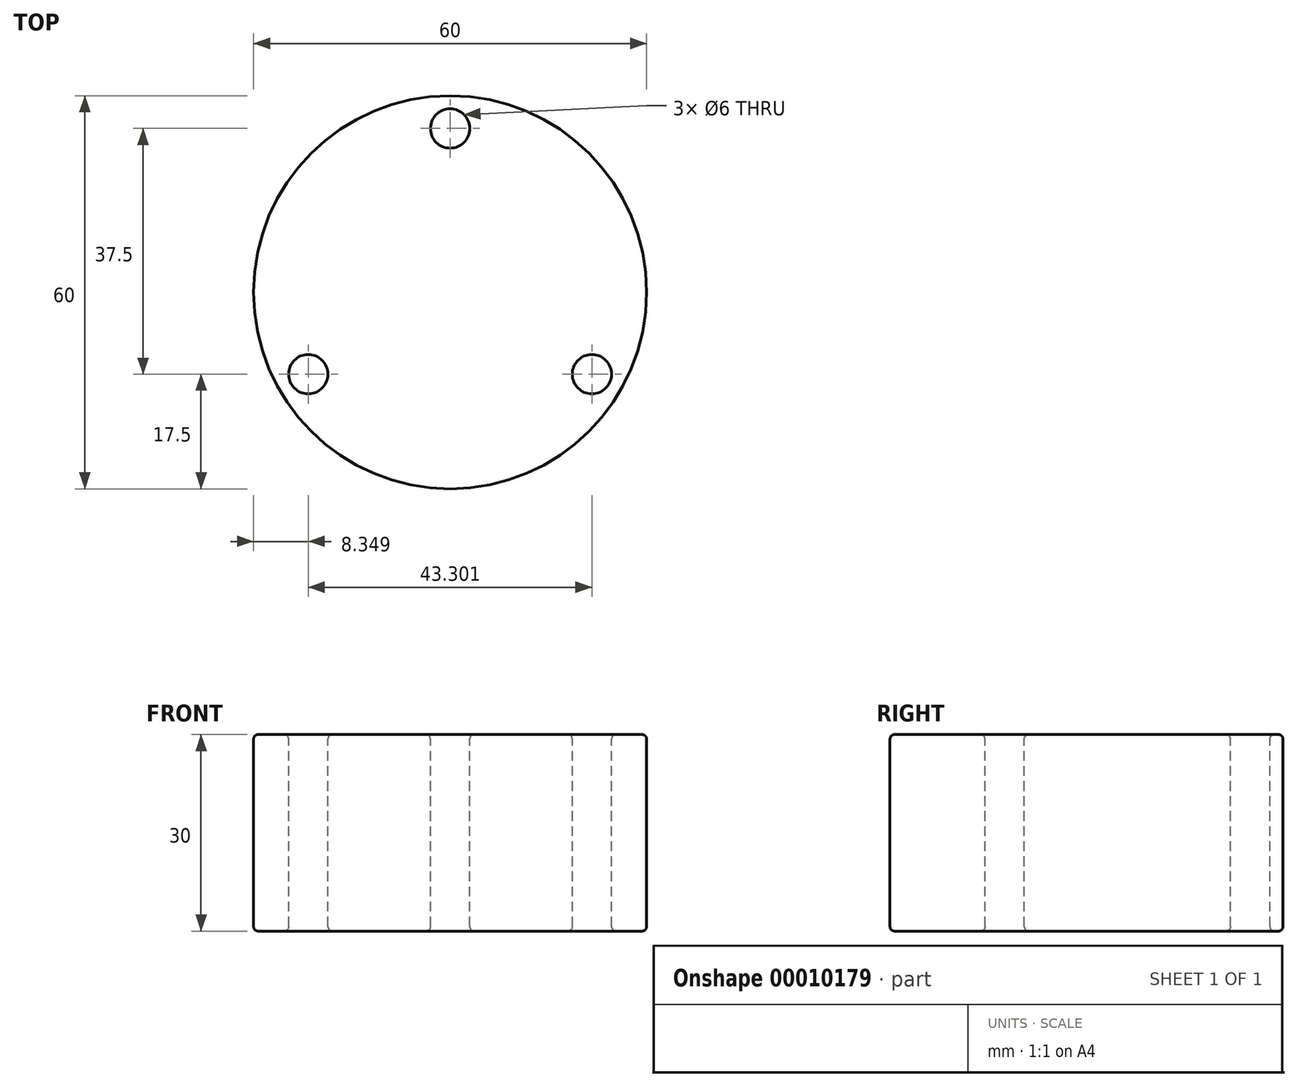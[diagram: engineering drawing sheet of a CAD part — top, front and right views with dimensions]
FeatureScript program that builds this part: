
annotation { "Feature Type Name" : "Feature", "Feature Type Description" : "" }
export const myFeature = defineFeature(function(context is Context, id is Id, definition is map)
    precondition{}
    {
        {
            var Q0;
            Q0=qCreatedBy(makeId("Top.planeOp"),FACE);
            var sketch = newSketch(context, id + "F0", { "sketchPlane" : qUnion([Q0])});
            skCircle(sketch, "E0", {"center": v(0, 0) * mm, "radius": 30 * mm});
            skCircle(sketch, "E1", {"center": v(0, 25) * mm, "radius": 3 * mm});
            skCircle(sketch, "E2.1.0", {"center": v(-21.65, -12.5) * mm, "radius": 3 * mm});
            skCircle(sketch, "E2.2.0", {"center": v(21.65, -12.5) * mm, "radius": 3 * mm});
            skSolve(sketch);
        }
        {
            var Q0;
            Q0=makeQuery(id+"F0.imprint","IMPRINT",FACE,{"disambiguationData":[TD([[makeQuery(id+"F0.imprint","IMPRINT",EDGE,{"derivedFrom":sQuery(id+"F0.wireOp",EDGE,"E0")}),1.0]])]});
            var Q1;
            Q1=sQuery(id+"F0.wireOp",EDGE,"E0");
            extrude(context, id + "F1", {"entities" : qUnion([Q0]), "surfaceEntities" : qUnion([Q1]), "oppositeDirection" : true, "depth" : 30 * mm});
        }
        {
            var Q0;
            Q0=makeQuery(id+"F1.opExtrude","CAP_EDGE",EDGE,{"disambiguationData":[OSD([sQuery(id+"F0.wireOp",EDGE,"E0")])],"isStart":true});
            var Q1;
            Q1=makeQuery(id+"F1.opExtrude","CAP_EDGE",EDGE,{"disambiguationData":[OSD([sQuery(id+"F0.wireOp",EDGE,"E2.1.0")])],"isStart":true});
            var Q2;
            Q2=makeQuery(id+"F1.opExtrude","CAP_EDGE",EDGE,{"disambiguationData":[OSD([sQuery(id+"F0.wireOp",EDGE,"E2.2.0")])],"isStart":true});
            var Q3;
            Q3=makeQuery(id+"F1.opExtrude","CAP_EDGE",EDGE,{"disambiguationData":[OSD([sQuery(id+"F0.wireOp",EDGE,"E1")])],"isStart":true});
            var Q4;
            Q4=makeQuery(id+"F1.opExtrude","CAP_EDGE",EDGE,{"disambiguationData":[OSD([sQuery(id+"F0.wireOp",EDGE,"E0")])],"isStart":false});
            var Q5;
            Q5=makeQuery(id+"F1.opExtrude","CAP_EDGE",EDGE,{"disambiguationData":[OSD([sQuery(id+"F0.wireOp",EDGE,"E2.1.0")])],"isStart":false});
            var Q6;
            Q6=makeQuery(id+"F1.opExtrude","CAP_EDGE",EDGE,{"disambiguationData":[OSD([sQuery(id+"F0.wireOp",EDGE,"E1")])],"isStart":false});
            var Q7;
            Q7=makeQuery(id+"F1.opExtrude","CAP_EDGE",EDGE,{"disambiguationData":[OSD([sQuery(id+"F0.wireOp",EDGE,"E2.2.0")])],"isStart":false});
            fillet(context, id + "F2", {"entities" : qUnion([Q0, Q1, Q2, Q3, Q4, Q5, Q6, Q7]), "radius" : 0.7 * mm, "tangentPropagation" : true, "allowEdgeOverflow" : false});
        }
    });
